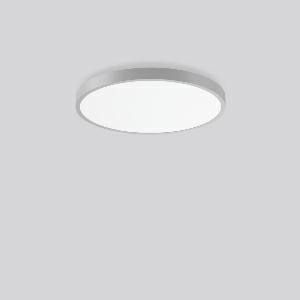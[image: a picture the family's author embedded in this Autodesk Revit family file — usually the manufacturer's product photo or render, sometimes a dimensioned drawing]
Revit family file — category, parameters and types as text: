
# Revit family: triona_round_a_312384_004_1_730_71bd
name_source: partatom
category: Lighting Fixtures
units: mm (PartAtom-declared; Revit-internal decimal feet)

## family parameters
Cut with Voids When Loaded = No
Host = Face
Light Source = No
Part Type = Normal
Room Calculation Point = No
Round Connector Dimension = Use Diameter
Shared = No

## types (1)
- TRIONA round A (1 x LED Modul 840, 9650 lm, 4000)
    Apparent Load = 106 VA
    CIE Flux Codes = 49 80 96 72 100
    Color Rendering = 80
    Color Temperature = 4000
    Default Elevation = 1800 mm
    Description = Series: TRIONA round
Decorative round LED surface-mounted luminaire. Flat, seamless frame: aluminium extrusion profile, powder coated. Cover made of sheet steel, powder-coated. Direct light emission through a diffuser plastic opal. Indirect light emission through a flush diffuser made of satin-finish plastic. Lightguide and diffuser made of non-yellowing plastic (PMMA). Lateral light emission (RZB SIDELITE technology) for above-average homogeneous light distribution. Direct 70%, indirect 30% light emission. Suitable for Ceiling mounting, Wall (surface). Tool-free mounting via bayonet connection. Electronic ballast included. Very easy installation thanks to Plug+Play connection. With Casambi smart+free Bluetooth control for wireless network and operation using Android / iOS devices, free app available for download. 
Colour: silver, matt (approx. RAL 9006)
Diameter: 681 mm
Height: 88 mm
Lamp: LED
Socket: without socket
Colour temperature: 4000K
Colour rendering index (CRI): 80
System power: 106 W
Rated luminous flux: 9650 lm
Luminous efficiency: 91 lm/W
Control gear: Dimmable Bluetooth converter
Protection class: I
Type of protection: IP 20
    Height = 88 mm  [stored 0.288714 ft]
    Lamp = 1 x LED Modul 840
    Lamp Light Flux = 9650 lm
    Lamp count = 1
    Length = 681 mm
    Lifetime = 50000 h
    Luminous efficacy = 91 lm/W
    Manufacturer = RZB
    ModVariant = No
    Model = 312384.004.1.730
    Mounting Place = Ceiling
    Mounting Type = Surface mounted
    Number of Poles = 1
    OnlyDefault = Yes
    Power Factor = 1
    Product Name = TRIONA round A
    Product group = Surface mounted modular luminaires
    ProductGroupID = 306
    Protection Class = Protection class I
    Protection Degree = IP 20
    RLX_Detail_Level = 1
    RLX_Emergency_Light_Flux = 0 lm
    RLX_Emergency_Type = 0
    RLX_Emergency_Type_DB = No
    RlxData = <blob elided: 42061 chars, md5=ef2c65e6>
    Socket = socket
    Standby Power = 0 W
    System Light Flux = 9650 lm
    System Power = 106 W
    Type Comments = Product without accessories
    Type Image = 312384.004.jpg
    URL = http://relux.com
    VarID = ---
    Voltage = 230 V
    Voltage Range = 220-240 V
    Weight = 0.00 kg
    Width = 0 mm  [stored 0 ft]

note: [stored X ft] marks values corroborated as IEEE doubles in the binary element streams (Revit-internal decimal feet)

## geometry (parser evidence)
native form markers: Blend x4, Sweep x11
no freeform markers — native parametric forms only
